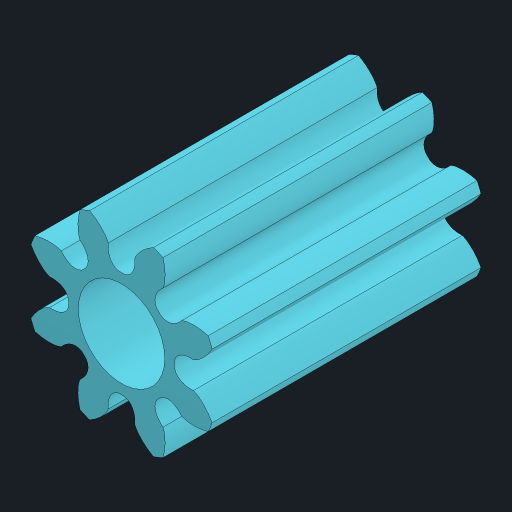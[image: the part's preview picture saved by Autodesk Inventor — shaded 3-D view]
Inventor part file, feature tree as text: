
AUTODESK INVENTOR PART (.ipt)
format: ipt  version: 2023.2 (Build 272271030, 271C)  size: 217,600 bytes
history: native  units: mm
features: sketch x2, extrude x2, pattern_circular x1, hole x1
ambient origin geometry x8: Origin, YZ Plane, XZ Plane, XY Plane, X Axis, Y Axis, Z Axis, Center Point
bodies: Solid1 (feature_tree)
feature tree (6):
  sketch  "Sketch1"  dims[d0=14.0mm d1=0.0mm d2=0.0mm d3=0.0mm]
  extrude  "Extrusion1"  TaperAngle=0.0deg  [1 undecoded]
  extrude  "Extrusion2"  TaperAngle=0.0deg  [1 undecoded]
  pattern_circular  "Circular Pattern1"  [2 undecoded]
  hole  "Hole1"  [1 undecoded]
  sketch  "Sketch2"  dims[d4=80.0mm d5=360.0deg d7=2.5mm d8=6.0mm d9=4.5mm d10=5.8mm d11=90.0deg d12=8.0mm d13=20.594885mm d17=0.0mm d18=0.0mm d19=0.0mm d20=0.0mm]
note: 5 required parameter values undecoded (feature->parameter linkage not recoverable at this tier; creation-order binding heuristic only, values carry confidence <= 0.55)
